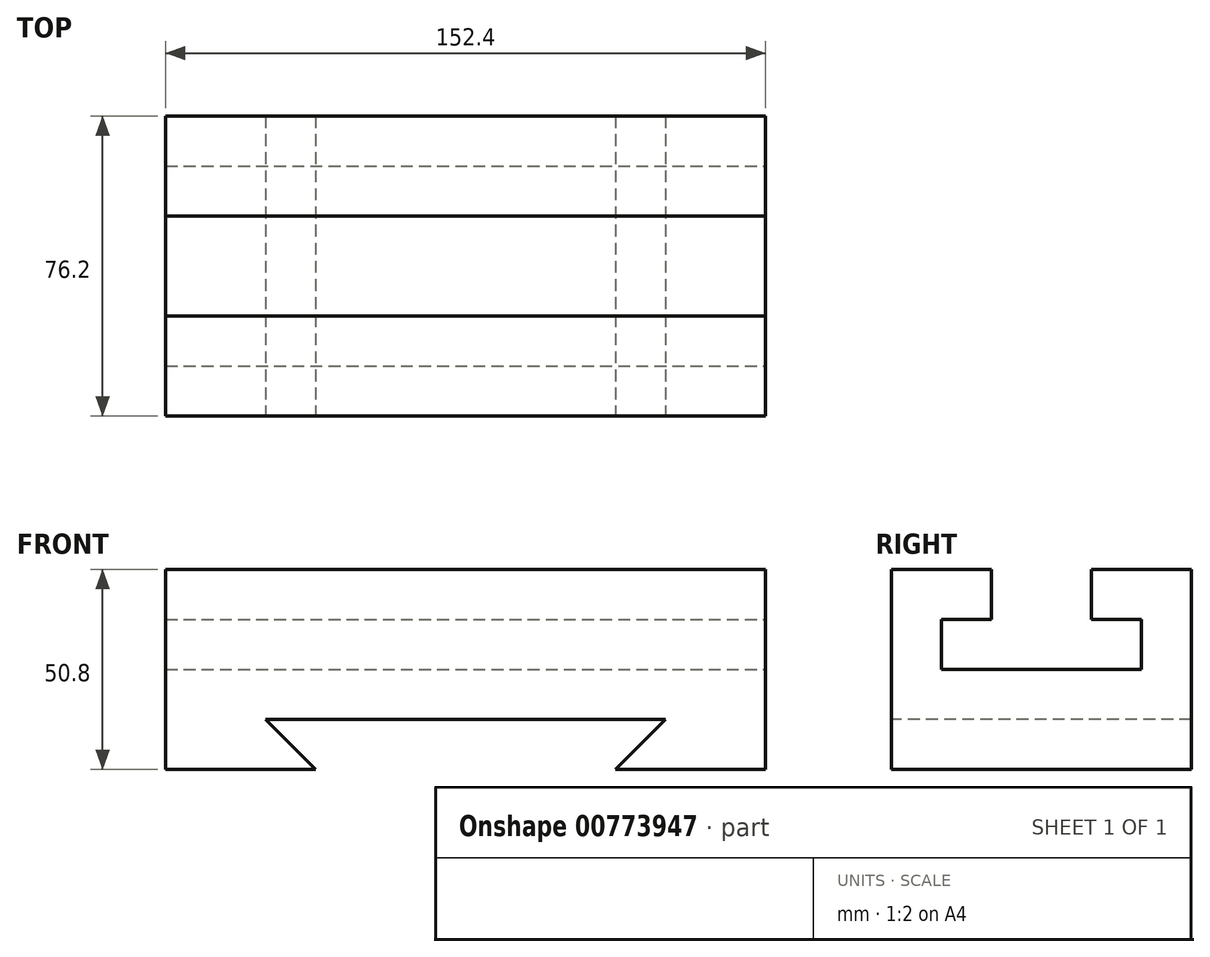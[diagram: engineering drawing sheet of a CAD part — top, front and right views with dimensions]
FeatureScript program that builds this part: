
annotation { "Feature Type Name" : "Feature", "Feature Type Description" : "" }
export const myFeature = defineFeature(function(context is Context, id is Id, definition is map)
    precondition{}
    {
        {
            var Q0;
            Q0=qCreatedBy(makeId("Front.planeOp"),FACE);
            var sketch = newSketch(context, id + "F0", { "sketchPlane" : qUnion([Q0])});
            skLineSegment(sketch, "E0", {"start": v(0, 0) * mm, "end": v(152.4, 0) * mm});
            skLineSegment(sketch, "E1", {"start": v(152.4, 0) * mm, "end": v(152.4, 50.8) * mm});
            skLineSegment(sketch, "E2", {"start": v(152.4, 50.8) * mm, "end": v(0, 50.8) * mm});
            skLineSegment(sketch, "E3", {"start": v(0, 50.8) * mm, "end": v(0, 0) * mm});
            skSolve(sketch);
        }
        {
            var Q0;
            Q0=makeQuery(id+"F0.imprint","IMPRINT",FACE,{"disambiguationData":[TD([[makeQuery(id+"F0.imprint","IMPRINT",EDGE,{"derivedFrom":sQuery(id+"F0.wireOp",EDGE,"E0")}),1.0]])]});
            extrude(context, id + "F1", {"entities" : qUnion([Q0]), "depth" : 76.2 * mm, "offsetDistance" : 25.4 * mm});
        }
        {
            var Q0;
            Q0=makeQuery(id+"F1.opExtrude","SWEPT_FACE",FACE,{"disambiguationData":[OSD([sQuery(id+"F0.wireOp",EDGE,"E2")])]});
            extrude(context, id + "F2", {"entities" : qUnion([Q0]), "operationType" : NewBodyOperationType.REMOVE, "oppositeDirection" : true, "depth" : 25.4 * mm, "offsetDistance" : 25.4 * mm});
        }
        {
            var Q0;
            Q0=makeQuery(id+"F2.boolean.opBoolean","COPY",FACE,{"derivedFrom":makeQuery(id+"F2.opExtrude","CAP_FACE",FACE,{"disambiguationData":[OSD([sQuery(id+"F0.wireOp",EDGE,"E2")])],"isStart":false})});
            var sketch = newSketch(context, id + "F3", { "sketchPlane" : qUnion([Q0])});
            skLineSegment(sketch, "E4", {"start": v(0, 0) * mm, "end": v(0, -12.7) * mm});
            skLineSegment(sketch, "E5", {"start": v(0, -12.7) * mm, "end": v(152.4, -12.7) * mm});
            skLineSegment(sketch, "E6", {"start": v(152.4, -12.7) * mm, "end": v(152.4, 0) * mm});
            skLineSegment(sketch, "E7", {"start": v(152.4, 0) * mm, "end": v(0, 0) * mm});
            skSolve(sketch);
        }
        {
            var Q0;
            Q0=makeQuery(id+"F3.imprint","IMPRINT",FACE,{"disambiguationData":[TD([[makeQuery(id+"F3.imprint","IMPRINT",EDGE,{"derivedFrom":sQuery(id+"F3.wireOp",EDGE,"E4")}),-1.0]])]});
            extrude(context, id + "F4", {"entities" : qUnion([Q0]), "operationType" : NewBodyOperationType.ADD, "depth" : 25.4 * mm, "offsetDistance" : 25.4 * mm});
        }
        {
            var Q0;
            Q0=makeQuery(id+"F4.opExtrude","SWEPT_FACE",FACE,{"disambiguationData":[OSD([sQuery(id+"F3.wireOp",EDGE,"E5")])]});
            var sketch = newSketch(context, id + "F5", { "sketchPlane" : qUnion([Q0])});
            skLineSegment(sketch, "E8", {"start": v(0, 50.8) * mm, "end": v(0, 38.1) * mm});
            skLineSegment(sketch, "E9", {"start": v(0, 38.1) * mm, "end": v(152.4, 38.1) * mm});
            skLineSegment(sketch, "E10", {"start": v(152.4, 38.1) * mm, "end": v(152.4, 50.8) * mm});
            skLineSegment(sketch, "E11", {"start": v(152.4, 50.8) * mm, "end": v(0, 50.8) * mm});
            skSolve(sketch);
        }
        {
            var Q0;
            Q0=makeQuery(id+"F5.imprint","IMPRINT",FACE,{"disambiguationData":[TD([[makeQuery(id+"F5.imprint","IMPRINT",EDGE,{"derivedFrom":sQuery(id+"F5.wireOp",EDGE,"E8")}),1.0]])]});
            extrude(context, id + "F6", {"entities" : qUnion([Q0]), "operationType" : NewBodyOperationType.ADD, "depth" : 12.7 * mm, "offsetDistance" : 25.4 * mm});
        }
        {
            var Q0;
            Q0=makeQuery(id+"F2.boolean.opBoolean","COPY",FACE,{"derivedFrom":makeQuery(id+"F2.opExtrude","CAP_FACE",FACE,{"disambiguationData":[OSD([sQuery(id+"F0.wireOp",EDGE,"E2")])],"isStart":false})});
            var sketch = newSketch(context, id + "F7", { "sketchPlane" : qUnion([Q0])});
            skLineSegment(sketch, "E12", {"start": v(0, -76.2) * mm, "end": v(0, -63.5) * mm});
            skLineSegment(sketch, "E13", {"start": v(0, -63.5) * mm, "end": v(152.4, -63.5) * mm});
            skLineSegment(sketch, "E14", {"start": v(152.4, -63.5) * mm, "end": v(152.4, -76.2) * mm});
            skLineSegment(sketch, "E15", {"start": v(152.4, -76.2) * mm, "end": v(0, -76.2) * mm});
            skSolve(sketch);
        }
        {
            var Q0;
            Q0=makeQuery(id+"F7.imprint","IMPRINT",FACE,{"disambiguationData":[TD([[makeQuery(id+"F7.imprint","IMPRINT",EDGE,{"derivedFrom":sQuery(id+"F7.wireOp",EDGE,"E12")}),-1.0]])]});
            extrude(context, id + "F8", {"entities" : qUnion([Q0]), "operationType" : NewBodyOperationType.ADD, "depth" : 25.4 * mm, "offsetDistance" : 25.4 * mm});
        }
        {
            var Q0;
            Q0=makeQuery(id+"F8.opExtrude","SWEPT_FACE",FACE,{"disambiguationData":[OSD([sQuery(id+"F7.wireOp",EDGE,"E13")])]});
            var sketch = newSketch(context, id + "F9", { "sketchPlane" : qUnion([Q0])});
            skLineSegment(sketch, "E16", {"start": v(-152.4, 50.8) * mm, "end": v(-152.4, 38.1) * mm});
            skLineSegment(sketch, "E17", {"start": v(-152.4, 38.1) * mm, "end": v(0, 38.1) * mm});
            skLineSegment(sketch, "E18", {"start": v(0, 38.1) * mm, "end": v(0, 50.8) * mm});
            skLineSegment(sketch, "E19", {"start": v(0, 50.8) * mm, "end": v(-152.4, 50.8) * mm});
            skSolve(sketch);
        }
        {
            var Q0;
            Q0=makeQuery(id+"F9.imprint","IMPRINT",FACE,{"disambiguationData":[TD([[makeQuery(id+"F9.imprint","IMPRINT",EDGE,{"derivedFrom":sQuery(id+"F9.wireOp",EDGE,"E16")}),1.0]])]});
            extrude(context, id + "F10", {"entities" : qUnion([Q0]), "operationType" : NewBodyOperationType.ADD, "depth" : 12.7 * mm, "offsetDistance" : 25.4 * mm});
        }
        {
            var Q0;
            Q0=makeQuery(id+"F8.boolean.opBoolean","MERGE",FACE,{"derivedFrom":[makeQuery(id+"F1.opExtrude","CAP_FACE",FACE,{"disambiguationData":[OSD([sQuery(id+"F0.wireOp",EDGE,"E0"),sQuery(id+"F0.wireOp",EDGE,"E1"),sQuery(id+"F0.wireOp",EDGE,"E2"),sQuery(id+"F0.wireOp",EDGE,"E3")])],"isStart":false}),makeQuery(id+"F8.opExtrude","SWEPT_FACE",FACE,{"disambiguationData":[OSD([sQuery(id+"F7.wireOp",EDGE,"E15")])]})]});
            var sketch = newSketch(context, id + "F11", { "sketchPlane" : qUnion([Q0])});
            skLineSegment(sketch, "E20", {"start": v(38.1, 0) * mm, "end": v(25.4, 12.7) * mm});
            skLineSegment(sketch, "E21", {"start": v(25.4, 12.7) * mm, "end": v(127, 12.7) * mm});
            skLineSegment(sketch, "E22", {"start": v(114.3, 0) * mm, "end": v(127, 12.7) * mm});
            skLineSegment(sketch, "E23", {"start": v(38.1, 0) * mm, "end": v(114.3, 0) * mm});
            skSolve(sketch);
        }
        {
            var Q0;
            Q0=makeQuery(id+"F11.imprint","IMPRINT",FACE,{"disambiguationData":[TD([[makeQuery(id+"F11.imprint","IMPRINT",EDGE,{"derivedFrom":sQuery(id+"F11.wireOp",EDGE,"E20")}),-1.0]])]});
            extrude(context, id + "F12", {"entities" : qUnion([Q0]), "operationType" : NewBodyOperationType.REMOVE, "oppositeDirection" : true, "depth" : 76.2 * mm, "offsetDistance" : 25.4 * mm});
        }
    });
